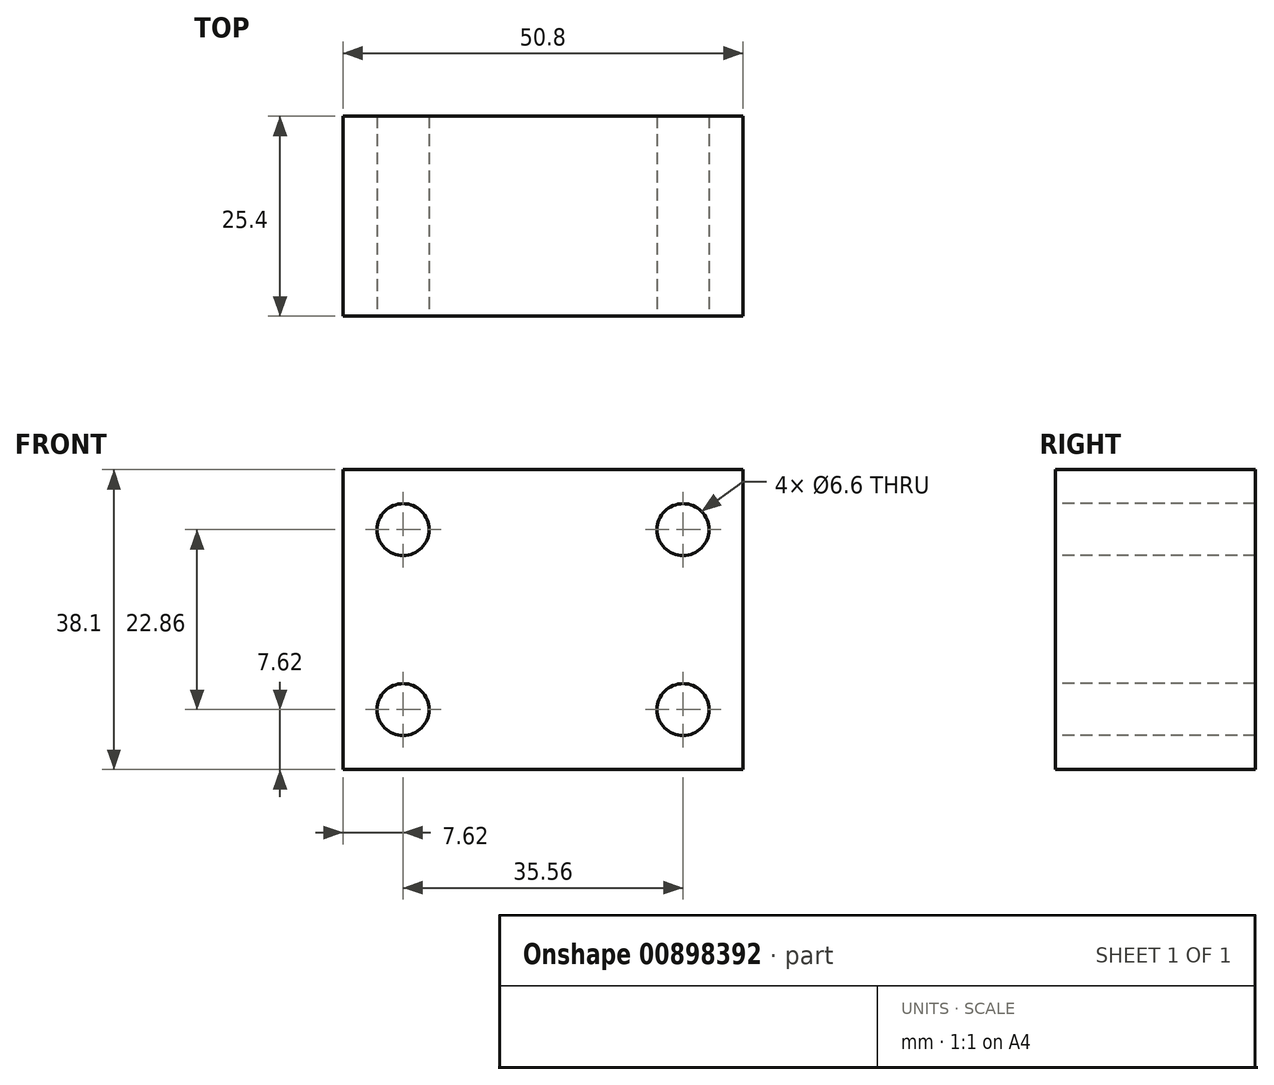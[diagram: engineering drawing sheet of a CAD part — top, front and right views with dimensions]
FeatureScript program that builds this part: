
annotation { "Feature Type Name" : "Feature", "Feature Type Description" : "" }
export const myFeature = defineFeature(function(context is Context, id is Id, definition is map)
    precondition{}
    {
        {
            var Q0;
            Q0=qCreatedBy(makeId("Front.planeOp"),FACE);
            var sketch = newSketch(context, id + "F0", { "sketchPlane" : qUnion([Q0])});
            skLineSegment(sketch, "E0.bottom", {"start": v(0, 0) * mm, "end": v(50.8, 0) * mm});
            skLineSegment(sketch, "E0.top", {"start": v(0, 38.1) * mm, "end": v(50.8, 38.1) * mm});
            skLineSegment(sketch, "E0.left", {"start": v(0, 0) * mm, "end": v(0, 38.1) * mm});
            skLineSegment(sketch, "E0.right", {"start": v(50.8, 0) * mm, "end": v(50.8, 38.1) * mm});
            skSolve(sketch);
        }
        {
            var Q0;
            Q0 = qSketchRegion(id + "F0", true);
            extrude(context, id + "F1", {"entities" : qUnion([Q0]), "depth" : 25.4 * mm, "offsetDistance" : 25.4 * mm});
        }
        {
            var Q0;
            Q0=makeQuery(id+"F1.opExtrude","CAP_FACE",FACE,{"disambiguationData":[OSD([sQuery(id+"F0.wireOp",EDGE,"E0.bottom"),sQuery(id+"F0.wireOp",EDGE,"E0.top"),sQuery(id+"F0.wireOp",EDGE,"E0.left"),sQuery(id+"F0.wireOp",EDGE,"E0.right")])],"isStart":false});
            var sketch = newSketch(context, id + "F2", { "sketchPlane" : qUnion([Q0])});
            skPoint(sketch, "E1", {"position": v(7.62, 30.48) * mm});
            skPoint(sketch, "E2", {"position": v(43.18, 30.48) * mm});
            skPoint(sketch, "E3", {"position": v(7.62, 7.62) * mm});
            skPoint(sketch, "E4", {"position": v(43.18, 7.62) * mm});
            skSolve(sketch);
        }
        {
            var Q0;
            Q0=sQuery(id+"F2.wireOp",VERTEX,"E1");
            var Q1;
            Q1=sQuery(id+"F2.wireOp",VERTEX,"E2");
            var Q2;
            Q2=sQuery(id+"F2.wireOp",VERTEX,"E3");
            var Q3;
            Q3=sQuery(id+"F2.wireOp",VERTEX,"E4");
            var Q4;
            Q4=makeQuery(id+"F1.opExtrude","SWEPT_BODY",BODY,{"disambiguationData":[OSD([sQuery(id+"F0.wireOp",EDGE,"E0.bottom"),sQuery(id+"F0.wireOp",EDGE,"E0.top"),sQuery(id+"F0.wireOp",EDGE,"E0.left"),sQuery(id+"F0.wireOp",EDGE,"E0.right")])]});
            hole(context, id + "F3", {"style" : HoleStyle.SIMPLE, "endStyle" : HoleEndStyle.THROUGH, "standardTappedOrClearance" : lookupTablePath({ "fit" : "Normal", "standard" : "ISO", "size" : "M6", "type" : "Clearance" }), "standardBlindInLast" : lookupTablePath({ "fit" : "Normal", "standard" : "ISO", "size" : "M6", "type" : "Clearance" }), "holeDiameter" : 6.6 * mm, "majorDiameter" : 6.35 * mm, "isTappedThrough" : true, "tappedDepth" : 12.7 * mm, "tapClearance" : 3, "locations" : qUnion([Q0, Q1, Q2, Q3]), "scope" : qUnion([Q4])});
        }
    });
